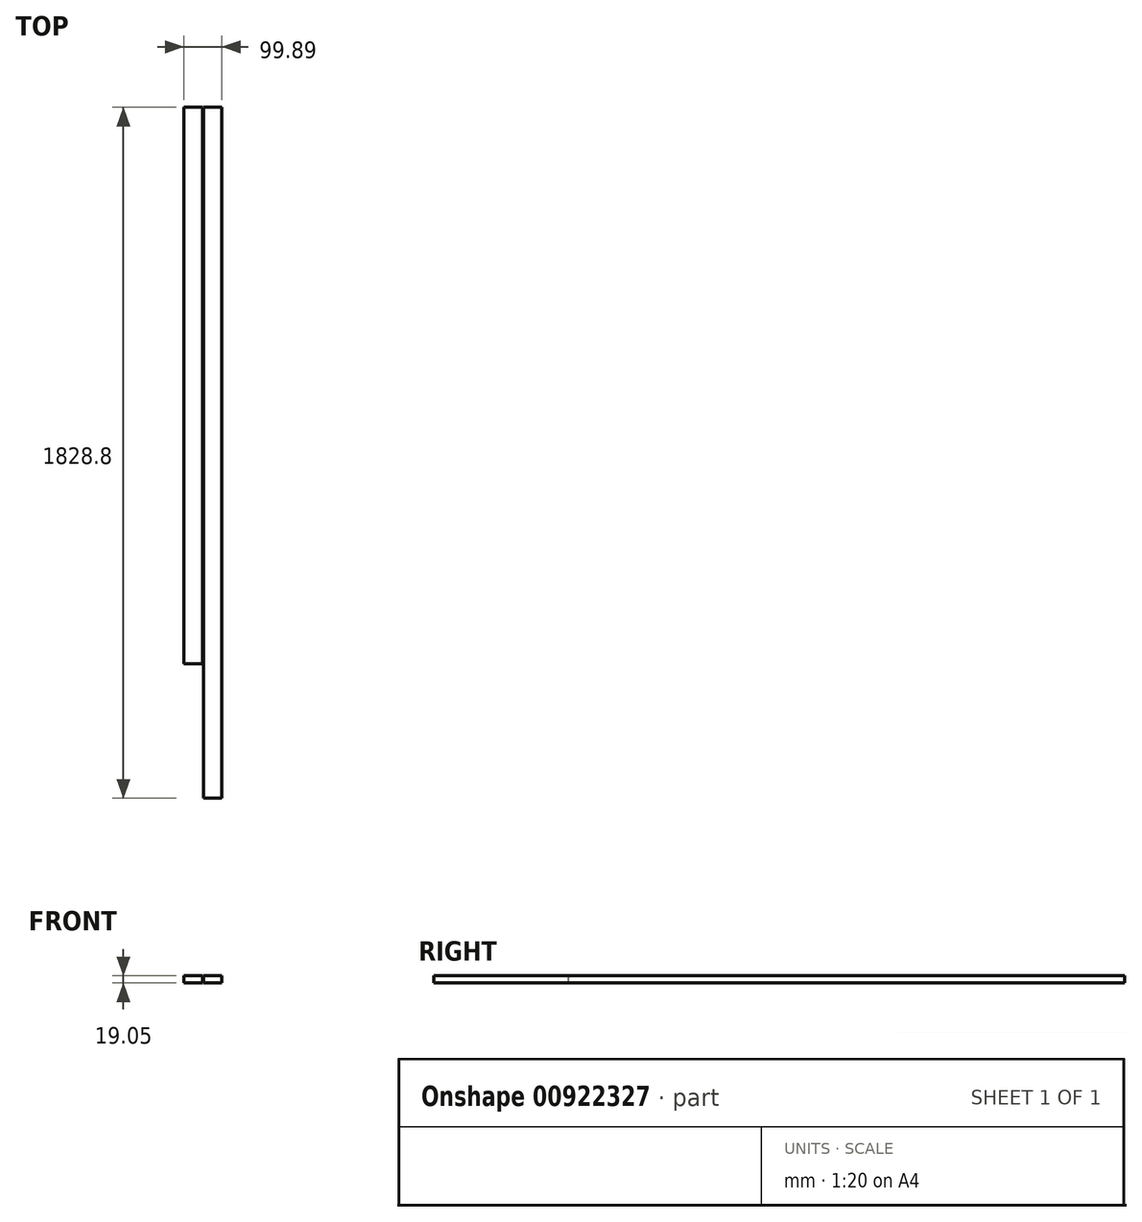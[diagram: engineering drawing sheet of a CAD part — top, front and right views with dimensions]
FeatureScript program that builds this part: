
annotation { "Feature Type Name" : "Feature", "Feature Type Description" : "" }
export const myFeature = defineFeature(function(context is Context, id is Id, definition is map)
    precondition{}
    {
        {
            var Q0;
            Q0=qCreatedBy(makeId("Front.planeOp"),FACE);
            var sketch = newSketch(context, id + "F0", { "sketchPlane" : qUnion([Q0])});
            skLineSegment(sketch, "E0.bottom", {"start": v(-2.83, 0) * mm, "end": v(45.57, 0) * mm});
            skLineSegment(sketch, "E0.top", {"start": v(-2.83, 19.05) * mm, "end": v(45.57, 19.05) * mm});
            skLineSegment(sketch, "E0.left", {"start": v(-2.83, 0) * mm, "end": v(-2.83, 19.05) * mm});
            skLineSegment(sketch, "E0.right", {"start": v(45.57, 0) * mm, "end": v(45.57, 19.05) * mm});
            skSolve(sketch);
        }
        {
            var Q0;
            Q0=makeQuery(id+"F0.imprint","IMPRINT",FACE,{"disambiguationData":[TD([[makeQuery(id+"F0.imprint","IMPRINT",EDGE,{"derivedFrom":sQuery(id+"F0.wireOp",EDGE,"E0.bottom")}),1.0]])]});
            extrude(context, id + "F1", {"entities" : qUnion([Q0]), "depth" : 1828.8 * mm, "offsetDistance" : 25.4 * mm});
        }
        {
            var Q0;
            Q0=qCreatedBy(makeId("Front.planeOp"),FACE);
            var sketch = newSketch(context, id + "F2", { "sketchPlane" : qUnion([Q0])});
            skLineSegment(sketch, "E1.bottom", {"start": v(-54.32, 19.05) * mm, "end": v(-4.54, 19.05) * mm});
            skLineSegment(sketch, "E1.top", {"start": v(-54.32, 0) * mm, "end": v(-4.54, 0) * mm});
            skLineSegment(sketch, "E1.left", {"start": v(-54.32, 19.05) * mm, "end": v(-54.32, 0) * mm});
            skLineSegment(sketch, "E1.right", {"start": v(-4.54, 19.05) * mm, "end": v(-4.54, 0) * mm});
            skSolve(sketch);
        }
        {
            var Q0;
            Q0=makeQuery(id+"F2.imprint","IMPRINT",FACE,{"disambiguationData":[TD([[makeQuery(id+"F2.imprint","IMPRINT",EDGE,{"derivedFrom":sQuery(id+"F2.wireOp",EDGE,"E1.bottom")}),-1.0]])]});
            var Q1;
            Q1 = qSketchRegion(id + "F2", true);
            extrude(context, id + "F3", {"entities" : qUnion([Q0, Q1]), "depth" : 1473.2 * mm, "offsetDistance" : 25.4 * mm});
        }
    });
